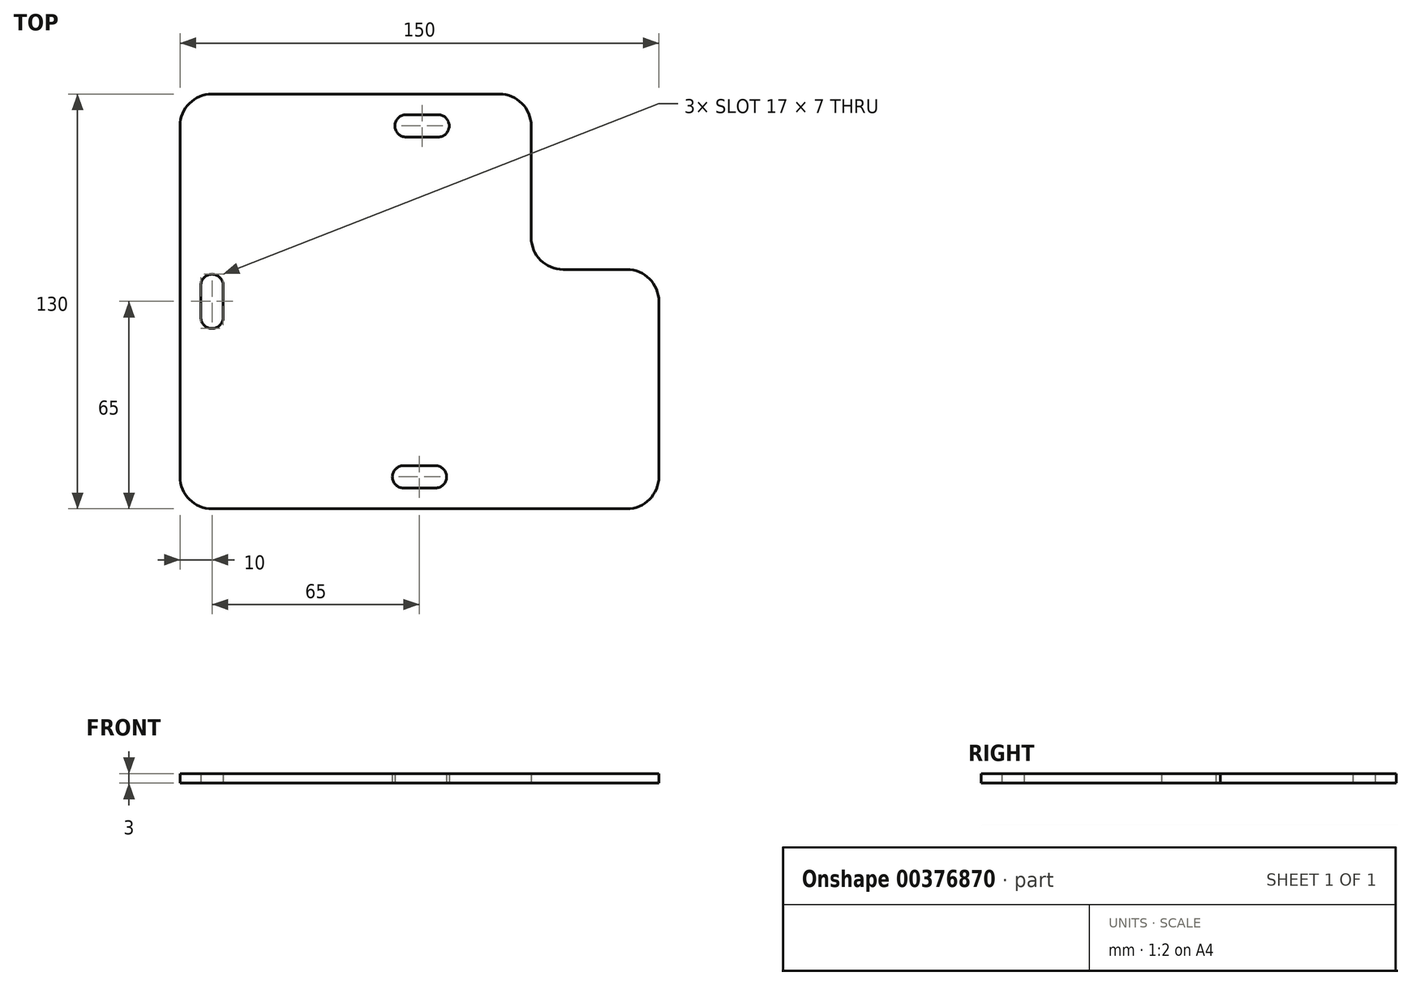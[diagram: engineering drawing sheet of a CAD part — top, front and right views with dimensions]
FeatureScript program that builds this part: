
annotation { "Feature Type Name" : "Feature", "Feature Type Description" : "" }
export const myFeature = defineFeature(function(context is Context, id is Id, definition is map)
    precondition{}
    {
        {
            var Q0;
            Q0=qCreatedBy(makeId("Top.planeOp"),FACE);
            var sketch = newSketch(context, id + "F0", { "sketchPlane" : qUnion([Q0])});
            skLineSegment(sketch, "E0.bottom", {"start": v(74.19, -65) * mm, "end": v(-55.81, -65) * mm});
            skLineSegment(sketch, "E0.top", {"start": v(34.19, 65) * mm, "end": v(-55.81, 65) * mm});
            skLineSegment(sketch, "E0.right", {"start": v(-65.81, -55) * mm, "end": v(-65.81, 55) * mm});
            skPoint(sketch, "E0.middle", {"position": v(0, 0) * mm});
            skLineSegment(sketch, "E1", {"start": v(4.19, -55) * mm, "end": v(14.19, -55) * mm, "construction": true});
            skLineSegment(sketch, "E2", {"start": v(-55.81, 5) * mm, "end": v(-55.81, -5) * mm, "construction": true});
            skLineSegment(sketch, "E3", {"start": v(5, 55) * mm, "end": v(15, 55) * mm, "construction": true});
            skArc(sketch, "E4.0.startCap", {"start": v(-59.31, 5) * mm, "mid": v(-55.81, 8.5) * mm, "end": v(-52.31, 5) * mm});
            skArc(sketch, "E4.0.endCap", {"start": v(-52.31, -5) * mm, "mid": v(-55.81, -8.5) * mm, "end": v(-59.31, -5) * mm});
            skLineSegment(sketch, "E4.0.left", {"start": v(-52.31, 5) * mm, "end": v(-52.31, -5) * mm});
            skLineSegment(sketch, "E4.0.right", {"start": v(-59.31, 5) * mm, "end": v(-59.31, -5) * mm});
            skArc(sketch, "E5.0.startCap", {"start": v(5, 51.5) * mm, "mid": v(1.5, 55) * mm, "end": v(5, 58.5) * mm});
            skArc(sketch, "E5.0.endCap", {"start": v(15, 58.5) * mm, "mid": v(18.5, 55) * mm, "end": v(15, 51.5) * mm});
            skLineSegment(sketch, "E5.0.left", {"start": v(5, 58.5) * mm, "end": v(15, 58.5) * mm});
            skLineSegment(sketch, "E5.0.right", {"start": v(5, 51.5) * mm, "end": v(15, 51.5) * mm});
            skArc(sketch, "E5.1.startCap", {"start": v(4.19, -58.5) * mm, "mid": v(0.69, -55) * mm, "end": v(4.19, -51.5) * mm});
            skArc(sketch, "E5.1.endCap", {"start": v(14.19, -51.5) * mm, "mid": v(17.69, -55) * mm, "end": v(14.19, -58.5) * mm});
            skLineSegment(sketch, "E5.1.left", {"start": v(4.19, -51.5) * mm, "end": v(14.19, -51.5) * mm});
            skLineSegment(sketch, "E5.1.right", {"start": v(4.19, -58.5) * mm, "end": v(14.19, -58.5) * mm});
            skArc(sketch, "E6.0.startCap", {"start": v(-59.31, 5) * mm, "mid": v(-55.81, 8.5) * mm, "end": v(-52.31, 5) * mm, "construction": true});
            skArc(sketch, "E6.0.endCap", {"start": v(-52.31, -5) * mm, "mid": v(-55.81, -8.5) * mm, "end": v(-59.31, -5) * mm, "construction": true});
            skLineSegment(sketch, "E6.0.left", {"start": v(-52.31, 5) * mm, "end": v(-52.31, -5) * mm, "construction": true});
            skLineSegment(sketch, "E6.0.right", {"start": v(-59.31, 5) * mm, "end": v(-59.31, -5) * mm, "construction": true});
            skArc(sketch, "E6.1.startCap", {"start": v(5, 51.5) * mm, "mid": v(1.5, 55) * mm, "end": v(5, 58.5) * mm, "construction": true});
            skArc(sketch, "E6.1.endCap", {"start": v(15, 58.5) * mm, "mid": v(18.5, 55) * mm, "end": v(15, 51.5) * mm, "construction": true});
            skLineSegment(sketch, "E6.1.left", {"start": v(5, 58.5) * mm, "end": v(15, 58.5) * mm, "construction": true});
            skLineSegment(sketch, "E6.1.right", {"start": v(5, 51.5) * mm, "end": v(15, 51.5) * mm, "construction": true});
            skArc(sketch, "E6.2.startCap", {"start": v(4.19, -58.5) * mm, "mid": v(0.69, -55) * mm, "end": v(4.19, -51.5) * mm, "construction": true});
            skArc(sketch, "E6.2.endCap", {"start": v(14.19, -51.5) * mm, "mid": v(17.69, -55) * mm, "end": v(14.19, -58.5) * mm, "construction": true});
            skLineSegment(sketch, "E6.2.left", {"start": v(4.19, -51.5) * mm, "end": v(14.19, -51.5) * mm, "construction": true});
            skLineSegment(sketch, "E6.2.right", {"start": v(4.19, -58.5) * mm, "end": v(14.19, -58.5) * mm, "construction": true});
            skPoint(sketch, "E7.visualSharp", {"position": v(65.81, 65) * mm});
            skPoint(sketch, "E8.visualSharp", {"position": v(-65.81, 65) * mm});
            skArc(sketch, "E8.filletArc", {"start": v(-55.81, 65) * mm, "mid": v(-62.88, 62.07) * mm, "end": v(-65.81, 55) * mm});
            skPoint(sketch, "E9.visualSharp", {"position": v(-65.81, -65) * mm});
            skArc(sketch, "E9.filletArc", {"start": v(-65.81, -55) * mm, "mid": v(-62.88, -62.07) * mm, "end": v(-55.81, -65) * mm});
            skPoint(sketch, "E10.visualSharp", {"position": v(65.81, -65) * mm});
            skPoint(sketch, "E11.visualSharp", {"position": v(30, 65) * mm});
            skPoint(sketch, "E12.visualSharp", {"position": v(30, -65) * mm});
            skPoint(sketch, "E13", {"position": v(10, 55) * mm});
            skPoint(sketch, "E14", {"position": v(9.19, -55) * mm});
            skLineSegment(sketch, "E15", {"start": v(84.19, 0) * mm, "end": v(84.19, -55) * mm});
            skLineSegment(sketch, "E16.bottom", {"start": v(74.19, 10) * mm, "end": v(54.19, 10) * mm});
            skLineSegment(sketch, "E16.right", {"start": v(44.19, 20) * mm, "end": v(44.19, 55) * mm});
            skPoint(sketch, "E16.middle", {"position": v(84.19, 50) * mm});
            skPoint(sketch, "E17.visualSharp", {"position": v(44.19, 10) * mm});
            skArc(sketch, "E17.filletArc", {"start": v(44.19, 20) * mm, "mid": v(47.12, 12.93) * mm, "end": v(54.19, 10) * mm});
            skArc(sketch, "E18.filletArc", {"start": v(44.19, 55) * mm, "mid": v(41.26, 62.07) * mm, "end": v(34.19, 65) * mm});
            skPoint(sketch, "E19.newPointB", {"position": v(124.19, 10) * mm});
            skArc(sketch, "E19.filletArc", {"start": v(84.19, 0) * mm, "mid": v(81.26, 7.07) * mm, "end": v(74.19, 10) * mm});
            skArc(sketch, "E20.filletArc", {"start": v(74.19, -65) * mm, "mid": v(81.26, -62.07) * mm, "end": v(84.19, -55) * mm});
            skPoint(sketch, "E21.visualSharp", {"position": v(124.19, 90) * mm});
            skSolve(sketch);
        }
        {
            var Q0;
            Q0=makeQuery(id+"F0.imprint","IMPRINT",FACE,{"disambiguationData":[TD([[makeQuery(id+"F0.imprint","IMPRINT",EDGE,{"derivedFrom":sQuery(id+"F0.wireOp",EDGE,"E0.bottom")}),-1.0]])]});
            extrude(context, id + "F1", {"entities" : qUnion([Q0]), "depth" : 3 * mm});
        }
    });
